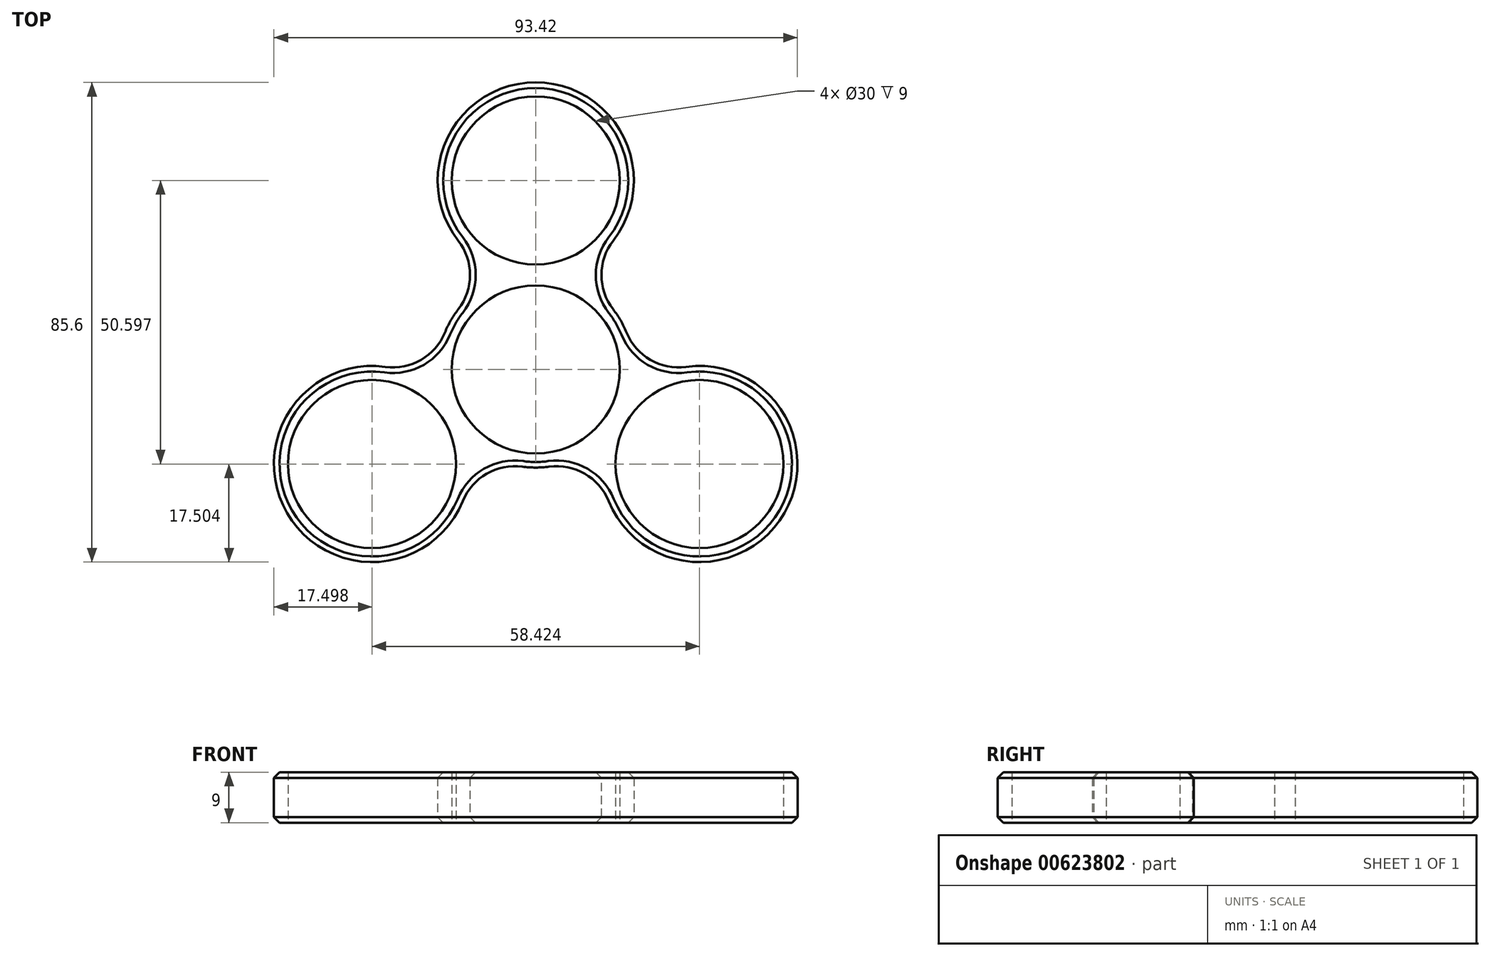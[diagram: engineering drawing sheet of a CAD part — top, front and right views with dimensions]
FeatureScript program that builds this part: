
annotation { "Feature Type Name" : "Feature", "Feature Type Description" : "" }
export const myFeature = defineFeature(function(context is Context, id is Id, definition is map)
    precondition{}
    {
        {
            var Q0;
            Q0=qCreatedBy(makeId("Top.planeOp"),FACE);
            var sketch = newSketch(context, id + "F0", { "sketchPlane" : qUnion([Q0])});
            skCircle(sketch, "E0", {"center": v(0, 0) * mm, "radius": 17.5 * mm});
            skSolve(sketch);
        }
        {
            var Q0;
            Q0=makeQuery(id+"F0.imprint","IMPRINT",FACE,{"disambiguationData":[TD([[makeQuery(id+"F0.imprint","IMPRINT",EDGE,{"derivedFrom":sQuery(id+"F0.wireOp",EDGE,"E0")}),1.0]])]});
            extrude(context, id + "F1", {"entities" : qUnion([Q0]), "depth" : 9 * mm, "offsetDistance" : 25 * mm});
        }
        {
            var Q0;
            Q0=qCreatedBy(makeId("Top.planeOp"),FACE);
            var sketch = newSketch(context, id + "F2", { "sketchPlane" : qUnion([Q0])});
            skCircle(sketch, "E1", {"center": v(0, 33.73) * mm, "radius": 17.5 * mm});
            skCircle(sketch, "E2.1.0", {"center": v(-29.21, -16.87) * mm, "radius": 17.5 * mm});
            skCircle(sketch, "E2.2.0", {"center": v(29.21, -16.87) * mm, "radius": 17.5 * mm});
            skPoint(sketch, "E2.center", {"position": v(0, 0) * mm});
            skSolve(sketch);
        }
        {
            var Q0;
            Q0=makeQuery(id+"F2.imprint","IMPRINT",FACE,{"disambiguationData":[TD([[makeQuery(id+"F2.imprint","IMPRINT",EDGE,{"derivedFrom":sQuery(id+"F2.wireOp",EDGE,"E1")}),1.0]])]});
            var Q1;
            Q1=makeQuery(id+"F2.imprint","IMPRINT",FACE,{"disambiguationData":[TD([[makeQuery(id+"F2.imprint","IMPRINT",EDGE,{"derivedFrom":sQuery(id+"F2.wireOp",EDGE,"E2.2.0")}),1.0]])]});
            var Q2;
            Q2=makeQuery(id+"F2.imprint","IMPRINT",FACE,{"disambiguationData":[TD([[makeQuery(id+"F2.imprint","IMPRINT",EDGE,{"derivedFrom":sQuery(id+"F2.wireOp",EDGE,"E2.1.0")}),1.0]])]});
            extrude(context, id + "F3", {"entities" : qUnion([Q0, Q1, Q2]), "operationType" : NewBodyOperationType.ADD, "depth" : 9 * mm, "offsetDistance" : 25 * mm});
        }
        {
            var Q0;
            Q0=makeQuery(id+"F3.boolean.opBoolean","MERGE",FACE,{"derivedFrom":[makeQuery(id+"F1.opExtrude","CAP_FACE",FACE,{"disambiguationData":[OSD([sQuery(id+"F0.wireOp",EDGE,"E0")])],"isStart":true}),makeQuery(id+"F3.opExtrude","CAP_FACE",FACE,{"disambiguationData":[OSD([sQuery(id+"F2.wireOp",EDGE,"E1")])],"isStart":true}),makeQuery(id+"F3.opExtrude","CAP_FACE",FACE,{"disambiguationData":[OSD([sQuery(id+"F2.wireOp",EDGE,"E2.1.0")])],"isStart":true}),makeQuery(id+"F3.opExtrude","CAP_FACE",FACE,{"disambiguationData":[OSD([sQuery(id+"F2.wireOp",EDGE,"E2.2.0")])],"isStart":true})]});
            var sketch = newSketch(context, id + "F4", { "sketchPlane" : qUnion([Q0])});
            skCircle(sketch, "E3", {"center": v(0, -33.73) * mm, "radius": 15 * mm});
            skSolve(sketch);
        }
        {
            var Q0;
            Q0=makeQuery(id+"F4.imprint","IMPRINT",FACE,{"disambiguationData":[TD([[makeQuery(id+"F4.imprint","IMPRINT",EDGE,{"derivedFrom":sQuery(id+"F4.wireOp",EDGE,"E3")}),-1.0]])]});
            var sketch = newSketch(context, id + "F5", { "sketchPlane" : qUnion([Q0])});
            skCircle(sketch, "E4", {"center": v(0, 0) * mm, "radius": 15 * mm});
            skSolve(sketch);
        }
        {
            var Q0;
            Q0=makeQuery(id+"F4.imprint","IMPRINT",FACE,{"disambiguationData":[TD([[makeQuery(id+"F4.imprint","IMPRINT",EDGE,{"derivedFrom":sQuery(id+"F4.wireOp",EDGE,"E3")}),1.0]])]});
            extrude(context, id + "F6", {"entities" : qUnion([Q0]), "operationType" : NewBodyOperationType.REMOVE, "oppositeDirection" : true, "depth" : 25 * mm, "offsetDistance" : 25 * mm});
        }
        {
            var Q0;
            Q0=makeQuery(id+"F5.imprint","IMPRINT",FACE,{"disambiguationData":[TD([[makeQuery(id+"F5.imprint","IMPRINT",EDGE,{"derivedFrom":sQuery(id+"F5.wireOp",EDGE,"E4")}),1.0]])]});
            extrude(context, id + "F7", {"entities" : qUnion([Q0]), "operationType" : NewBodyOperationType.REMOVE, "oppositeDirection" : true, "depth" : 25 * mm, "offsetDistance" : 25 * mm});
        }
        {
            var Q0;
            Q0=makeQuery(id+"F3.boolean.opBoolean","MERGE",FACE,{"derivedFrom":[makeQuery(id+"F1.opExtrude","CAP_FACE",FACE,{"disambiguationData":[OSD([sQuery(id+"F0.wireOp",EDGE,"E0")])],"isStart":true}),makeQuery(id+"F3.opExtrude","CAP_FACE",FACE,{"disambiguationData":[OSD([sQuery(id+"F2.wireOp",EDGE,"E1")])],"isStart":true}),makeQuery(id+"F3.opExtrude","CAP_FACE",FACE,{"disambiguationData":[OSD([sQuery(id+"F2.wireOp",EDGE,"E2.1.0")])],"isStart":true}),makeQuery(id+"F3.opExtrude","CAP_FACE",FACE,{"disambiguationData":[OSD([sQuery(id+"F2.wireOp",EDGE,"E2.2.0")])],"isStart":true})]});
            var sketch = newSketch(context, id + "F8", { "sketchPlane" : qUnion([Q0])});
            skCircle(sketch, "E5", {"center": v(-29.21, 16.87) * mm, "radius": 15 * mm});
            skSolve(sketch);
        }
        {
            var Q0;
            Q0=makeQuery(id+"F8.imprint","IMPRINT",FACE,{"disambiguationData":[TD([[makeQuery(id+"F8.imprint","IMPRINT",EDGE,{"derivedFrom":sQuery(id+"F8.wireOp",EDGE,"E5")}),1.0]])]});
            extrude(context, id + "F9", {"entities" : qUnion([Q0]), "operationType" : NewBodyOperationType.REMOVE, "oppositeDirection" : true, "depth" : 25 * mm, "offsetDistance" : 25 * mm});
        }
        {
            var Q0;
            Q0=makeQuery(id+"F3.boolean.opBoolean","MERGE",FACE,{"derivedFrom":[makeQuery(id+"F1.opExtrude","CAP_FACE",FACE,{"disambiguationData":[OSD([sQuery(id+"F0.wireOp",EDGE,"E0")])],"isStart":true}),makeQuery(id+"F3.opExtrude","CAP_FACE",FACE,{"disambiguationData":[OSD([sQuery(id+"F2.wireOp",EDGE,"E1")])],"isStart":true}),makeQuery(id+"F3.opExtrude","CAP_FACE",FACE,{"disambiguationData":[OSD([sQuery(id+"F2.wireOp",EDGE,"E2.1.0")])],"isStart":true}),makeQuery(id+"F3.opExtrude","CAP_FACE",FACE,{"disambiguationData":[OSD([sQuery(id+"F2.wireOp",EDGE,"E2.2.0")])],"isStart":true})]});
            var sketch = newSketch(context, id + "F10", { "sketchPlane" : qUnion([Q0])});
            skCircle(sketch, "E6", {"center": v(29.21, 16.87) * mm, "radius": 15 * mm});
            skSolve(sketch);
        }
        {
            var Q0;
            Q0=makeQuery(id+"F10.imprint","IMPRINT",FACE,{"disambiguationData":[TD([[makeQuery(id+"F10.imprint","IMPRINT",EDGE,{"derivedFrom":sQuery(id+"F10.wireOp",EDGE,"E6")}),1.0]])]});
            extrude(context, id + "F11", {"entities" : qUnion([Q0]), "operationType" : NewBodyOperationType.REMOVE, "oppositeDirection" : true, "depth" : 25 * mm, "offsetDistance" : 25 * mm});
        }
        {
            var Q0;
            Q0=makeQuery(id+"F3.boolean.opBoolean","INTERSECT",EDGE,{"disambiguationData":[OD(1.0)],"derivedFrom":[makeQuery(id+"F1.opExtrude","SWEPT_FACE",FACE,{"disambiguationData":[OSD([sQuery(id+"F0.wireOp",EDGE,"E0")])]}),makeQuery(id+"F3.opExtrude","SWEPT_FACE",FACE,{"disambiguationData":[OSD([sQuery(id+"F2.wireOp",EDGE,"E2.2.0")])]})]});
            var Q1;
            Q1=makeQuery(id+"F3.boolean.opBoolean","INTERSECT",EDGE,{"disambiguationData":[OD(1.0)],"derivedFrom":[makeQuery(id+"F1.opExtrude","SWEPT_FACE",FACE,{"disambiguationData":[OSD([sQuery(id+"F0.wireOp",EDGE,"E0")])]}),makeQuery(id+"F3.opExtrude","SWEPT_FACE",FACE,{"disambiguationData":[OSD([sQuery(id+"F2.wireOp",EDGE,"E2.1.0")])]})]});
            var Q2;
            Q2=makeQuery(id+"F3.boolean.opBoolean","INTERSECT",EDGE,{"disambiguationData":[OD(0.0)],"derivedFrom":[makeQuery(id+"F1.opExtrude","SWEPT_FACE",FACE,{"disambiguationData":[OSD([sQuery(id+"F0.wireOp",EDGE,"E0")])]}),makeQuery(id+"F3.opExtrude","SWEPT_FACE",FACE,{"disambiguationData":[OSD([sQuery(id+"F2.wireOp",EDGE,"E2.1.0")])]})]});
            var Q3;
            Q3=makeQuery(id+"F3.boolean.opBoolean","INTERSECT",EDGE,{"disambiguationData":[OD(0.0)],"derivedFrom":[makeQuery(id+"F1.opExtrude","SWEPT_FACE",FACE,{"disambiguationData":[OSD([sQuery(id+"F0.wireOp",EDGE,"E0")])]}),makeQuery(id+"F3.opExtrude","SWEPT_FACE",FACE,{"disambiguationData":[OSD([sQuery(id+"F2.wireOp",EDGE,"E1")])]})]});
            var Q4;
            Q4=makeQuery(id+"F3.boolean.opBoolean","INTERSECT",EDGE,{"disambiguationData":[OD(1.0)],"derivedFrom":[makeQuery(id+"F1.opExtrude","SWEPT_FACE",FACE,{"disambiguationData":[OSD([sQuery(id+"F0.wireOp",EDGE,"E0")])]}),makeQuery(id+"F3.opExtrude","SWEPT_FACE",FACE,{"disambiguationData":[OSD([sQuery(id+"F2.wireOp",EDGE,"E1")])]})]});
            var Q5;
            Q5=makeQuery(id+"F3.boolean.opBoolean","INTERSECT",EDGE,{"disambiguationData":[OD(0.0)],"derivedFrom":[makeQuery(id+"F1.opExtrude","SWEPT_FACE",FACE,{"disambiguationData":[OSD([sQuery(id+"F0.wireOp",EDGE,"E0")])]}),makeQuery(id+"F3.opExtrude","SWEPT_FACE",FACE,{"disambiguationData":[OSD([sQuery(id+"F2.wireOp",EDGE,"E2.2.0")])]})]});
            fillet(context, id + "F12", {"entities" : qUnion([Q0, Q1, Q2, Q3, Q4, Q5]), "radius" : 10 * mm, "tangentPropagation" : true, "allowEdgeOverflow" : false});
        }
        {
            var Q0;
            Q0=makeQuery(id+"F3.opExtrude","CAP_EDGE",EDGE,{"disambiguationData":[OSD([sQuery(id+"F2.wireOp",EDGE,"E2.2.0")])],"isStart":true});
            chamfer(context, id + "F13", {"entities" : qUnion([Q0]), "width" : 1 * mm, "tangentPropagation" : true});
        }
        {
            var Q0;
            Q0=makeQuery(id+"F3.opExtrude","CAP_EDGE",EDGE,{"disambiguationData":[OSD([sQuery(id+"F2.wireOp",EDGE,"E2.2.0")])],"isStart":false});
            chamfer(context, id + "F14", {"entities" : qUnion([Q0]), "width" : 1 * mm, "tangentPropagation" : true});
        }
    });
